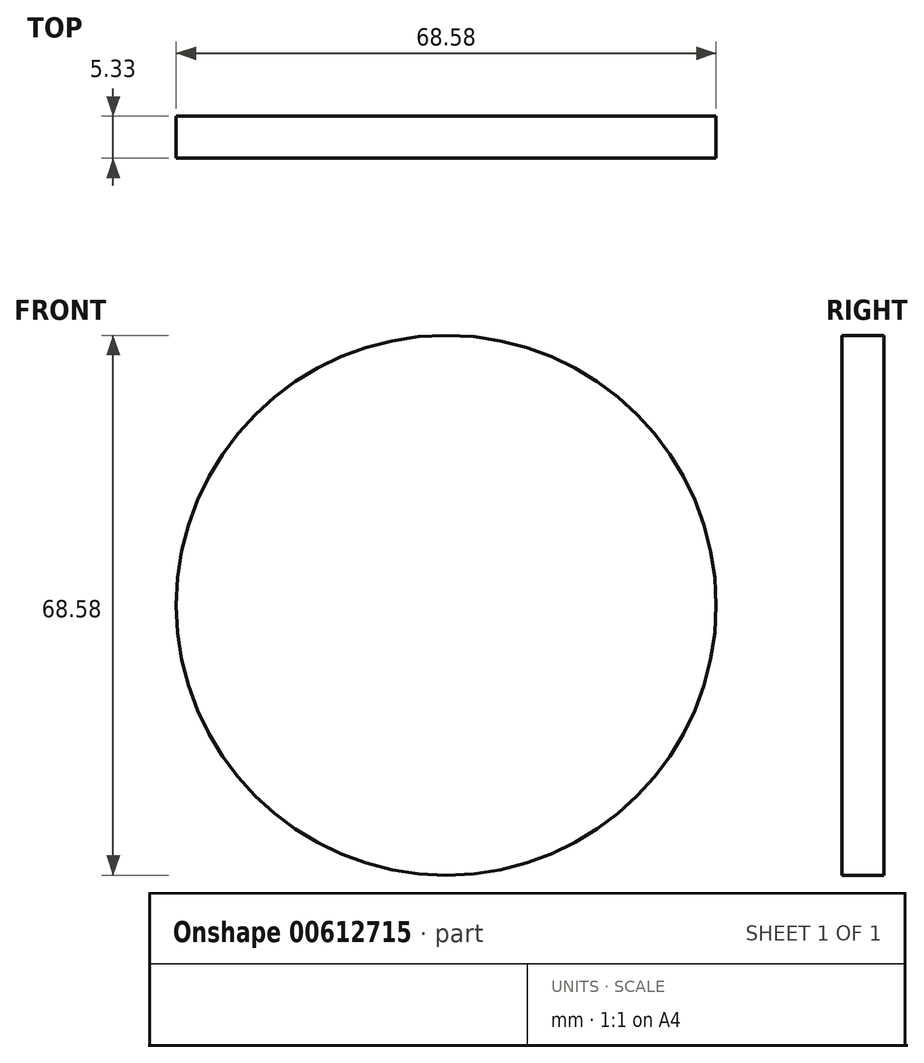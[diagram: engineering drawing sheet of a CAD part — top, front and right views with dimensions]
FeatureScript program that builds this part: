
annotation { "Feature Type Name" : "Feature", "Feature Type Description" : "" }
export const myFeature = defineFeature(function(context is Context, id is Id, definition is map)
    precondition{}
    {
        {
            var Q0;
            Q0=qCreatedBy(makeId("Front.planeOp"),FACE);
            var sketch = newSketch(context, id + "F0", { "sketchPlane" : qUnion([Q0])});
            skCircle(sketch, "E0", {"center": v(-20.33, -15.57) * mm, "radius": 34.29 * mm});
            skSolve(sketch);
        }
        {
            var Q0;
            Q0 = qSketchRegion(id + "F0", true);
            extrude(context, id + "F1", {"entities" : qUnion([Q0]), "oppositeDirection" : true, "depth" : 5.33 * mm, "offsetDistance" : 25.4 * mm});
        }
    });
